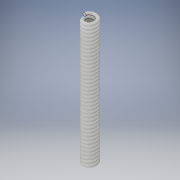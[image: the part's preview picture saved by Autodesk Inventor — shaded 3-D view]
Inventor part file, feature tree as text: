
AUTODESK INVENTOR PART (.ipt)
format: ipt  version: 2018 (Build 220112000, 112)  size: 546,816 bytes
history: native  units: in
note: dims shown in document units (in); Inventor stores cm internally (conversion verified against a paired STEP export)
features: helix x1, sketch x1
ambient origin geometry x8: Origin, YZ Plane, XZ Plane, XY Plane, X Axis, Y Axis, Z Axis, Center Point
bodies: Solid1 (feature_tree)
feature tree (2):
  helix  "Coil1"  [1 undecoded]
  sketch  "Sketch1"  dims[d1=0.044in d2=1.0in d3=0.7717in d4=14.9606in d5=0.0in d6=0.0in d7=0.0in d8=0.0in d9=0.0in]
note: 1 required parameter value undecoded (feature->parameter linkage not recoverable at this tier; creation-order binding heuristic only, values carry confidence <= 0.55)
